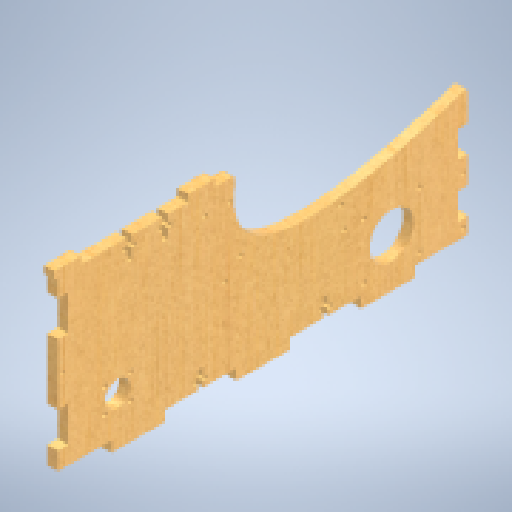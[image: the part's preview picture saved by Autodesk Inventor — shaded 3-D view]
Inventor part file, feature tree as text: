
AUTODESK INVENTOR PART (.ipt)
format: ipt  version: 2024.2 (Build 282272000, 272)  size: 716,288 bytes
history: native  units: mm
features: extrude x14, sketch x14, other x4, fillet x1, reference x1
ambient origin geometry x8: Origin, YZ Plane, XZ Plane, XY Plane, X Axis, Y Axis, Z Axis, Center Point
bodies: Body1 (feature_tree)
feature tree (34):
  other  "Твердое тело1"
  extrude  "Выдавливание1"  Depth=230.0mm
  extrude  "Выдавливание2"  Depth=100.0mm
  extrude  "Выдавливание3"  Depth=6.0mm TaperAngle=0.0deg
  extrude  "Выдавливание4"  Depth=30.0mm
  extrude  "Выдавливание5"  Depth=30.0mm
  extrude  "Выдавливание6"  Depth=40.0mm
  extrude  "Выдавливание7"  Depth=30.0mm
  extrude  "Выдавливание8"  Depth=30.0mm
  extrude  "Выдавливание9"  Depth=40.0mm
  fillet  "Сопряжение1"  [1 undecoded]
  extrude  "Выдавливание11"  Depth=6.0mm
  extrude  "Выдавливание12"  Depth=6.0mm
  extrude  "Выдавливание13"  Depth=10.0mm
  extrude  "Выдавливание14"  Depth=10.0mm
  extrude  "Выдавливание10"  Depth=20.0mm
  sketch  "Эскиз1"
  sketch  "Эскиз2"
  sketch  "Эскиз3"
  sketch  "Эскиз4"
  sketch  "Эскиз5"
  sketch  "Эскиз6"
  sketch  "Эскиз7"
  sketch  "Эскиз8"
  sketch  "Эскиз9"
  sketch  "Эскиз10"
  sketch  "Эскиз11"
  sketch  "Эскиз12"
  reference  "Ссылка1"
  sketch  "Эскиз13"
  sketch  "Эскиз14"
  other  "<userpath>\Documents\Artist-v2\3D\Робот.iam"
  other  "Робот.iam"
  other  "крышка:1"
note: 1 required parameter value undecoded (feature->parameter linkage not recoverable at this tier; creation-order binding heuristic only, values carry confidence <= 0.55)
